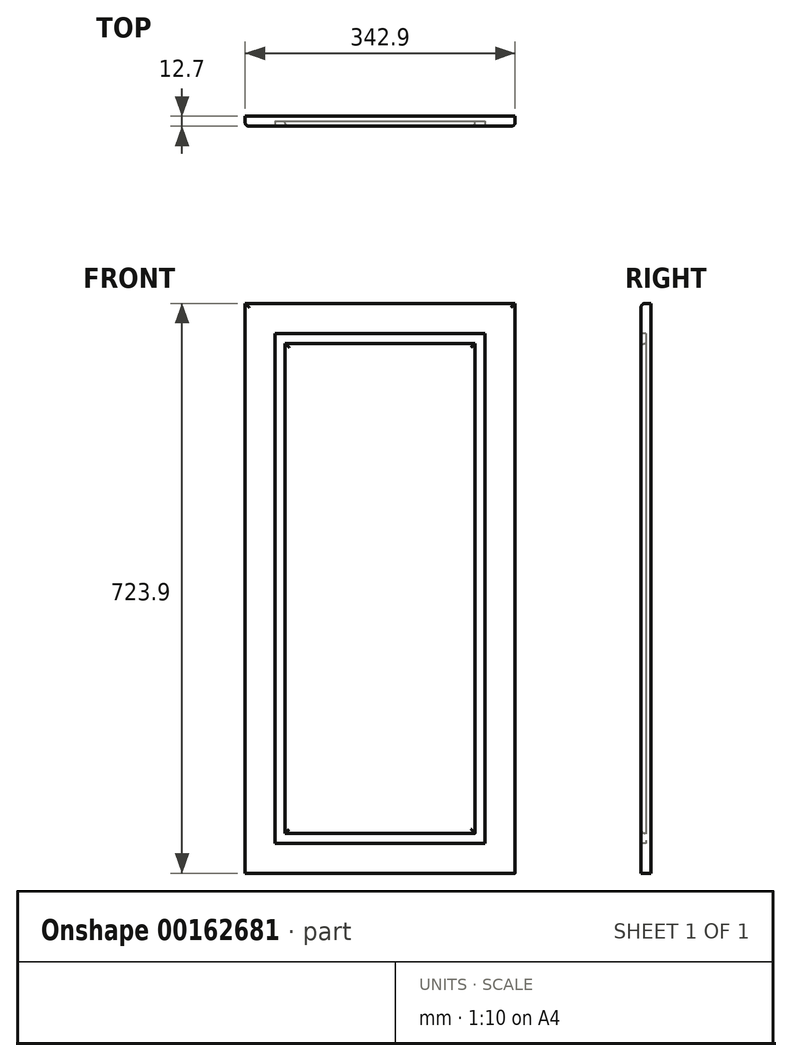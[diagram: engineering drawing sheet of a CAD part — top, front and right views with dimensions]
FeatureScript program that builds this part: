
annotation { "Feature Type Name" : "Feature", "Feature Type Description" : "" }
export const myFeature = defineFeature(function(context is Context, id is Id, definition is map)
    precondition{}
    {
        {
            var Q0;
            Q0=qCreatedBy(makeId("Front.planeOp"),FACE);
            var sketch = newSketch(context, id + "F0", { "sketchPlane" : qUnion([Q0])});
            skLineSegment(sketch, "E0.bottom", {"start": v(-217.1, 353.62) * mm, "end": v(125.8, 353.62) * mm});
            skLineSegment(sketch, "E0.top", {"start": v(-217.1, -370.28) * mm, "end": v(125.8, -370.28) * mm});
            skLineSegment(sketch, "E0.left", {"start": v(-217.1, 353.62) * mm, "end": v(-217.1, -370.28) * mm});
            skLineSegment(sketch, "E0.right", {"start": v(125.8, 353.62) * mm, "end": v(125.8, -370.28) * mm});
            skSolve(sketch);
        }
        {
            var Q0;
            Q0 = qSketchRegion(id + "F0", true);
            extrude(context, id + "F1", {"entities" : qUnion([Q0]), "depth" : 12.7 * mm});
        }
        {
            var Q0;
            Q0=makeQuery(id+"F1.opExtrude","CAP_FACE",FACE,{"disambiguationData":[OSD([sQuery(id+"F0.wireOp",EDGE,"E0.bottom"),sQuery(id+"F0.wireOp",EDGE,"E0.top"),sQuery(id+"F0.wireOp",EDGE,"E0.left"),sQuery(id+"F0.wireOp",EDGE,"E0.right")])],"isStart":false});
            var sketch = newSketch(context, id + "F2", { "sketchPlane" : qUnion([Q0])});
            skLineSegment(sketch, "E1.bottom", {"start": v(-179, 315.52) * mm, "end": v(87.7, 315.52) * mm});
            skLineSegment(sketch, "E1.top", {"start": v(-179, -332.18) * mm, "end": v(87.7, -332.18) * mm});
            skLineSegment(sketch, "E1.left", {"start": v(-179, 315.52) * mm, "end": v(-179, -332.18) * mm});
            skLineSegment(sketch, "E1.right", {"start": v(87.7, 315.52) * mm, "end": v(87.7, -332.18) * mm});
            skLineSegment(sketch, "E2.bottom", {"start": v(-166.3, 302.82) * mm, "end": v(75, 302.82) * mm});
            skLineSegment(sketch, "E2.top", {"start": v(-166.3, -319.48) * mm, "end": v(75, -319.48) * mm});
            skLineSegment(sketch, "E2.left", {"start": v(-166.3, 302.82) * mm, "end": v(-166.3, -319.48) * mm});
            skLineSegment(sketch, "E2.right", {"start": v(75, 302.82) * mm, "end": v(75, -319.48) * mm});
            skSolve(sketch);
        }
        {
            var Q0;
            Q0 = qSketchRegion(id + "F2", true);
            extrude(context, id + "F3", {"entities" : qUnion([Q0]), "operationType" : NewBodyOperationType.REMOVE, "oppositeDirection" : true, "depth" : 6.35 * mm});
        }
        {
            var Q0;
            Q0=makeQuery(id+"F1.opExtrude","CAP_EDGE",EDGE,{"disambiguationData":[OSD([sQuery(id+"F0.wireOp",EDGE,"E0.left")])],"isStart":false});
            var Q1;
            Q1=makeQuery(id+"F1.opExtrude","CAP_EDGE",EDGE,{"disambiguationData":[OSD([sQuery(id+"F0.wireOp",EDGE,"E0.bottom")])],"isStart":false});
            var Q2;
            Q2=makeQuery(id+"F1.opExtrude","CAP_EDGE",EDGE,{"disambiguationData":[OSD([sQuery(id+"F0.wireOp",EDGE,"E0.right")])],"isStart":false});
            var Q3;
            Q3=makeQuery(id+"F3.boolean.opBoolean","COPY",EDGE,{"derivedFrom":makeQuery(id+"F3.opExtrude","CAP_EDGE",EDGE,{"disambiguationData":[OSD([sQuery(id+"F2.wireOp",EDGE,"E1.right")])],"isStart":true})});
            var Q4;
            Q4=makeQuery(id+"F3.boolean.opBoolean","COPY",EDGE,{"derivedFrom":makeQuery(id+"F3.opExtrude","CAP_EDGE",EDGE,{"disambiguationData":[OSD([sQuery(id+"F2.wireOp",EDGE,"E1.bottom")])],"isStart":true})});
            var Q5;
            Q5=makeQuery(id+"F3.boolean.opBoolean","COPY",EDGE,{"derivedFrom":makeQuery(id+"F3.opExtrude","CAP_EDGE",EDGE,{"disambiguationData":[OSD([sQuery(id+"F2.wireOp",EDGE,"E1.left")])],"isStart":true})});
            var Q6;
            Q6=makeQuery(id+"F3.boolean.opBoolean","COPY",EDGE,{"derivedFrom":makeQuery(id+"F3.opExtrude","CAP_EDGE",EDGE,{"disambiguationData":[OSD([sQuery(id+"F2.wireOp",EDGE,"E2.left")])],"isStart":true})});
            var Q7;
            Q7=makeQuery(id+"F3.boolean.opBoolean","COPY",EDGE,{"derivedFrom":makeQuery(id+"F3.opExtrude","CAP_EDGE",EDGE,{"disambiguationData":[OSD([sQuery(id+"F2.wireOp",EDGE,"E2.bottom")])],"isStart":true})});
            var Q8;
            Q8=makeQuery(id+"F3.boolean.opBoolean","COPY",EDGE,{"derivedFrom":makeQuery(id+"F3.opExtrude","CAP_EDGE",EDGE,{"disambiguationData":[OSD([sQuery(id+"F2.wireOp",EDGE,"E2.right")])],"isStart":true})});
            var Q9;
            Q9=makeQuery(id+"F3.boolean.opBoolean","COPY",EDGE,{"derivedFrom":makeQuery(id+"F3.opExtrude","CAP_EDGE",EDGE,{"disambiguationData":[OSD([sQuery(id+"F2.wireOp",EDGE,"E2.top")])],"isStart":true})});
            var Q10;
            Q10=makeQuery(id+"F3.boolean.opBoolean","COPY",EDGE,{"derivedFrom":makeQuery(id+"F3.opExtrude","CAP_EDGE",EDGE,{"disambiguationData":[OSD([sQuery(id+"F2.wireOp",EDGE,"E1.top")])],"isStart":true})});
            fillet(context, id + "F4", {"entities" : qUnion([Q0, Q1, Q2, Q3, Q4, Q5, Q6, Q7, Q8, Q9, Q10]), "radius" : 5.08 * mm, "tangentPropagation" : true, "allowEdgeOverflow" : false});
        }
    });
